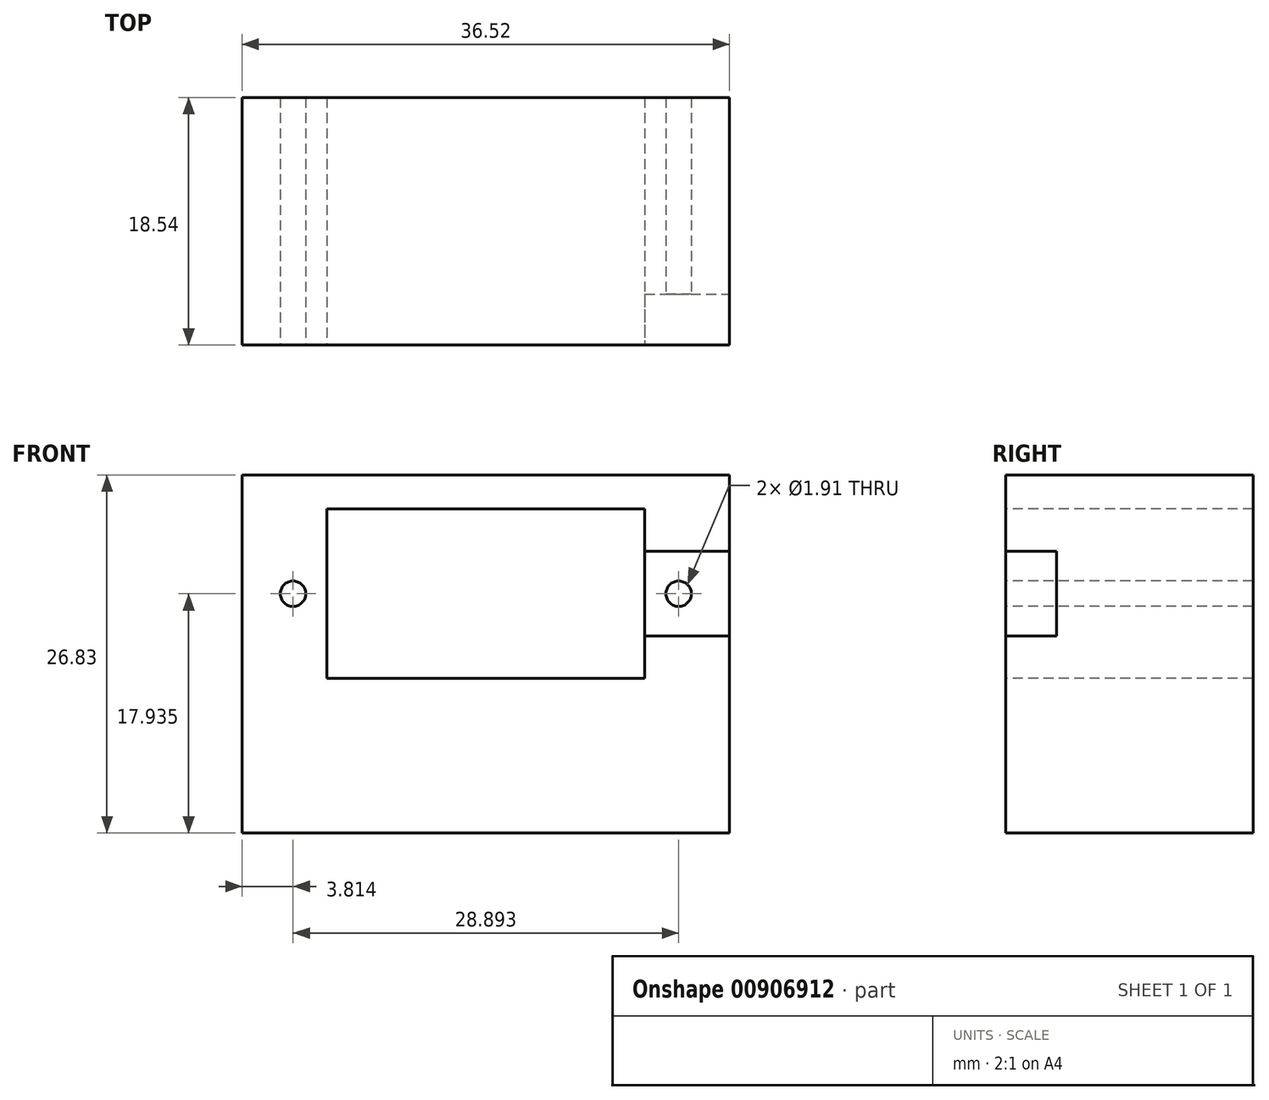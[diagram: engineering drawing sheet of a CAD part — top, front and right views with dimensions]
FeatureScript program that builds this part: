
annotation { "Feature Type Name" : "Feature", "Feature Type Description" : "" }
export const myFeature = defineFeature(function(context is Context, id is Id, definition is map)
    precondition{}
    {
        {
            var Q0;
            Q0=qCreatedBy(makeId("Top.planeOp"),FACE);
            var sketch = newSketch(context, id + "F0", { "sketchPlane" : qUnion([Q0])});
            skLineSegment(sketch, "E0.bottom", {"start": v(11.9, -6.35) * mm, "end": v(-11.9, -6.35) * mm});
            skLineSegment(sketch, "E0.top", {"start": v(11.9, 6.35) * mm, "end": v(-11.9, 6.35) * mm});
            skLineSegment(sketch, "E0.left", {"start": v(11.9, -6.35) * mm, "end": v(11.9, 6.35) * mm});
            skLineSegment(sketch, "E0.right", {"start": v(-11.9, -6.35) * mm, "end": v(-11.9, 6.35) * mm});
            skPoint(sketch, "E0.middle", {"position": v(0, 0) * mm});
            skLineSegment(sketch, "E1.bottom", {"start": v(18.26, -8.89) * mm, "end": v(-18.26, -8.9) * mm});
            skLineSegment(sketch, "E1.top", {"start": v(18.26, 8.9) * mm, "end": v(-18.26, 8.89) * mm});
            skLineSegment(sketch, "E1.left", {"start": v(18.26, -8.9) * mm, "end": v(18.26, 8.9) * mm});
            skLineSegment(sketch, "E1.right", {"start": v(-18.26, -8.9) * mm, "end": v(-18.26, 8.9) * mm});
            skLineSegment(sketch, "E2", {"start": v(11.9, -6.35) * mm, "end": v(18.26, -6.35) * mm});
            skLineSegment(sketch, "E3", {"start": v(-11.9, -6.35) * mm, "end": v(-18.26, -6.35) * mm});
            skLineSegment(sketch, "E4", {"start": v(-11.9, 6.35) * mm, "end": v(-18.26, 6.35) * mm});
            skLineSegment(sketch, "E5", {"start": v(11.9, 6.35) * mm, "end": v(18.26, 6.35) * mm});
            skLineSegment(sketch, "E6", {"start": v(18.26, -9.65) * mm, "end": v(-18.26, -9.65) * mm});
            skLineSegment(sketch, "E7", {"start": v(-18.26, -8.9) * mm, "end": v(-18.26, -9.65) * mm});
            skLineSegment(sketch, "E8", {"start": v(18.26, -8.89) * mm, "end": v(18.26, -9.65) * mm});
            skLineSegment(sketch, "E9", {"start": v(-18.26, -9.65) * mm, "end": v(-18.26, -12.2) * mm});
            skLineSegment(sketch, "E10", {"start": v(-18.26, -12.2) * mm, "end": v(18.26, -12.2) * mm});
            skLineSegment(sketch, "E11", {"start": v(18.26, -12.2) * mm, "end": v(18.26, -9.65) * mm});
            skLineSegment(sketch, "E12", {"start": v(-11.9, -6.35) * mm, "end": v(-11.9, -9.65) * mm});
            skLineSegment(sketch, "E13", {"start": v(11.9, -6.35) * mm, "end": v(11.9, -9.65) * mm});
            skSolve(sketch);
        }
        {
            var Q0;
            Q0=makeQuery(id+"F0.imprint","IMPRINT",FACE,{"disambiguationData":[TD([[makeQuery(id+"F0.imprint","IMPRINT",EDGE,{"derivedFrom":sQuery(id+"F0.wireOp",EDGE,"E0.right")}),1.0]])]});
            var Q1;
            Q1=makeQuery(id+"F0.imprint","IMPRINT",FACE,{"disambiguationData":[TD([[makeQuery(id+"F0.imprint","IMPRINT",EDGE,{"derivedFrom":sQuery(id+"F0.wireOp",EDGE,"E0.bottom")}),-1.0]])]});
            var Q2;
            Q2=makeQuery(id+"F0.imprint","IMPRINT",FACE,{"disambiguationData":[TD([[makeQuery(id+"F0.imprint","IMPRINT",EDGE,{"derivedFrom":sQuery(id+"F0.wireOp",EDGE,"E0.left")}),-1.0]])]});
            var Q3;
            {var subQ5=sQuery(id+"F0.wireOp",EDGE,"E3");Q3=makeQuery(id+"F0.imprint","IMPRINT",FACE,{"disambiguationData":[TD([[makeQuery(id+"F0.imprint","IMPRINT",EDGE,{"derivedFrom":subQ5}),1.0]])]});}
            var Q4;
            {var subQ0=sQuery(id+"F0.wireOp",EDGE,"E7");Q4=makeQuery(id+"F0.imprint","IMPRINT",FACE,{"disambiguationData":[TD([[makeQuery(id+"F0.imprint","IMPRINT",EDGE,{"derivedFrom":subQ0}),1.0]])]});}
            var Q5;
            {var subQ0=sQuery(id+"F0.wireOp",EDGE,"E9");Q5=makeQuery(id+"F0.imprint","IMPRINT",FACE,{"disambiguationData":[TD([[makeQuery(id+"F0.imprint","IMPRINT",EDGE,{"derivedFrom":subQ0}),1.0]])]});}
            var Q6;
            {var subQ0=sQuery(id+"F0.wireOp",EDGE,"E0.bottom");Q6=makeQuery(id+"F0.imprint","IMPRINT",FACE,{"disambiguationData":[TD([[makeQuery(id+"F0.imprint","IMPRINT",EDGE,{"derivedFrom":subQ0}),1.0]])]});}
            var Q7;
            {var subQ0=sQuery(id+"F0.wireOp",EDGE,"E13");var subQ1=sQuery(id+"F0.wireOp",EDGE,"E1.bottom");var subQ2=makeQuery(id+"F0.imprint","INTERSECT",VERTEX,{"derivedFrom":[subQ1,subQ0]});Q7=makeQuery(id+"F0.imprint","IMPRINT",FACE,{"disambiguationData":[TD([[makeQuery(id+"F0.imprint","IMPRINT",EDGE,{"disambiguationData":[TD([[subQ2,-1.0]])],"derivedFrom":subQ1}),1.0]])]});}
            var Q8;
            {var subQ5=sQuery(id+"F0.wireOp",EDGE,"E2");Q8=makeQuery(id+"F0.imprint","IMPRINT",FACE,{"disambiguationData":[TD([[makeQuery(id+"F0.imprint","IMPRINT",EDGE,{"derivedFrom":subQ5}),-1.0]])]});}
            var Q9;
            {var subQ0=sQuery(id+"F0.wireOp",EDGE,"E8");Q9=makeQuery(id+"F0.imprint","IMPRINT",FACE,{"disambiguationData":[TD([[makeQuery(id+"F0.imprint","IMPRINT",EDGE,{"derivedFrom":subQ0}),-1.0]])]});}
            extrude(context, id + "F1", {"entities" : qUnion([Q0, Q1, Q2, Q3, Q4, Q5, Q6, Q7, Q8, Q9]), "depth" : 30 * mm - 3.17 * mm, "offsetDistance" : 25.4 * mm});
        }
        {
            var Q0;
            Q0=makeQuery(id+"F1.opExtrude","SWEPT_FACE",FACE,{"disambiguationData":[OSD([sQuery(id+"F0.wireOp",EDGE,"E10")])]});
            var sketch = newSketch(context, id + "F2", { "sketchPlane" : qUnion([Q0])});
            skLineSegment(sketch, "E14.bottom", {"start": v(11.9, 24.28) * mm, "end": v(-11.9, 24.28) * mm});
            skLineSegment(sketch, "E14.top", {"start": v(11.9, 11.58) * mm, "end": v(-11.9, 11.58) * mm});
            skLineSegment(sketch, "E14.left", {"start": v(11.9, 24.28) * mm, "end": v(11.9, 11.58) * mm});
            skLineSegment(sketch, "E14.right", {"start": v(-11.9, 24.28) * mm, "end": v(-11.9, 11.58) * mm});
            skPoint(sketch, "E14.middle", {"position": v(0, 17.93) * mm});
            skLineSegment(sketch, "E15", {"start": v(-8.1, 24.28) * mm, "end": v(-8.1, 26.82) * mm});
            skLineSegment(sketch, "E16", {"start": v(8.1, 24.28) * mm, "end": v(8.1, 26.82) * mm});
            skCircle(sketch, "E17", {"center": v(-14.45, 17.93) * mm, "radius": 0.95 * mm});
            skCircle(sketch, "E18", {"center": v(14.45, 17.93) * mm, "radius": 0.95 * mm});
            skLineSegment(sketch, "E19", {"start": v(11.9, 14.76) * mm, "end": v(18.26, 14.76) * mm});
            skLineSegment(sketch, "E20", {"start": v(11.9, 21.1) * mm, "end": v(18.26, 21.1) * mm});
            skLineSegment(sketch, "E21", {"start": v(16.31, 21.1) * mm, "end": v(16.31, 14.76) * mm, "construction": true});
            skPoint(sketch, "E22", {"position": v(16.31, 17.93) * mm});
            skSolve(sketch);
        }
        {
            var Q0;
            Q0=makeQuery(id+"F2.imprint","IMPRINT",FACE,{"disambiguationData":[TD([[makeQuery(id+"F2.imprint","IMPRINT",EDGE,{"derivedFrom":sQuery(id+"F2.wireOp",EDGE,"E14.top")}),-1.0]])]});
            var Q1;
            Q1=makeQuery(id+"F2.imprint","IMPRINT",FACE,{"disambiguationData":[TD([[makeQuery(id+"F2.imprint","IMPRINT",EDGE,{"derivedFrom":sQuery(id+"F2.wireOp",EDGE,"E17")}),1.0]])]});
            var Q2;
            Q2=makeQuery(id+"F2.imprint","IMPRINT",FACE,{"disambiguationData":[TD([[makeQuery(id+"F2.imprint","IMPRINT",EDGE,{"derivedFrom":sQuery(id+"F2.wireOp",EDGE,"E18")}),1.0]])]});
            extrude(context, id + "F3", {"entities" : qUnion([Q0, Q1, Q2]), "operationType" : NewBodyOperationType.REMOVE, "endBound" : BoundingType.THROUGH_ALL, "oppositeDirection" : true, "depth" : 25.4 * mm, "offsetDistance" : 25.4 * mm});
        }
        {
            var Q0;
            Q0=makeQuery(id+"F2.imprint","IMPRINT",FACE,{"disambiguationData":[TD([[makeQuery(id+"F2.imprint","IMPRINT",EDGE,{"derivedFrom":sQuery(id+"F2.wireOp",EDGE,"E18")}),-1.0]])]});
            extrude(context, id + "F4", {"entities" : qUnion([Q0]), "operationType" : NewBodyOperationType.REMOVE, "oppositeDirection" : true, "depth" : 3.8 * mm, "offsetDistance" : 25.4 * mm});
        }
    });
